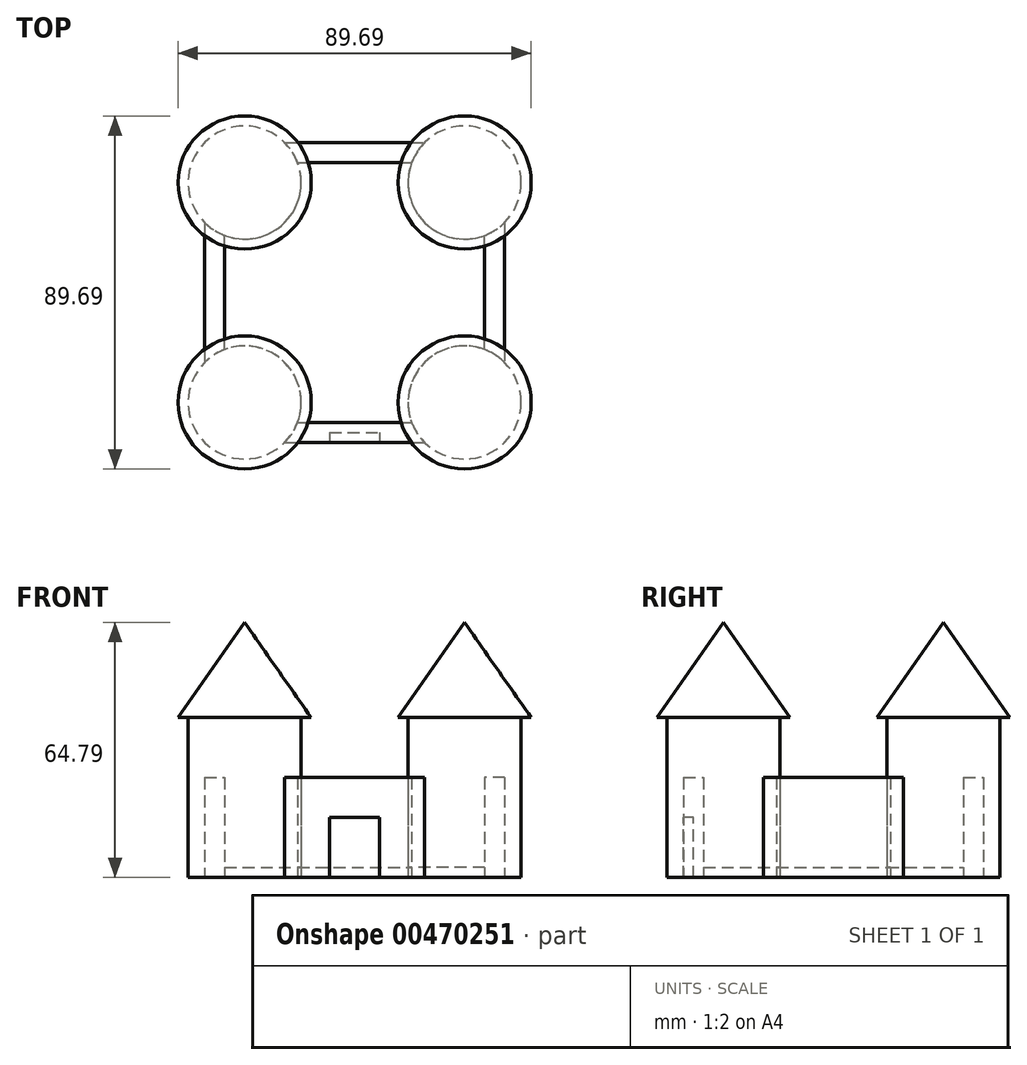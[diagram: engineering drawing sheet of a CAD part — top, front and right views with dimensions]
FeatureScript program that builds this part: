
annotation { "Feature Type Name" : "Feature", "Feature Type Description" : "" }
export const myFeature = defineFeature(function(context is Context, id is Id, definition is map)
    precondition{}
    {
        {
            var Q0;
            Q0=qCreatedBy(makeId("Top.planeOp"),FACE);
            var sketch = newSketch(context, id + "F0", { "sketchPlane" : qUnion([Q0])});
            skLineSegment(sketch, "E0.bottom", {"start": v(-37.26, 36.88) * mm, "end": v(38.94, 36.88) * mm});
            skLineSegment(sketch, "E0.top", {"start": v(-37.26, -39.32) * mm, "end": v(38.94, -39.32) * mm});
            skLineSegment(sketch, "E0.left", {"start": v(-37.26, 36.88) * mm, "end": v(-37.26, -39.32) * mm});
            skLineSegment(sketch, "E0.right", {"start": v(38.94, 36.88) * mm, "end": v(38.94, -39.32) * mm});
            skCircle(sketch, "E1", {"center": v(-27.1, 26.72) * mm, "radius": 14.37 * mm});
            skPoint(sketch, "E1.second.point", {"position": v(-37.26, 16.56) * mm});
            skPoint(sketch, "E1.third.point", {"position": v(-16.94, 36.88) * mm});
            skCircle(sketch, "E2", {"center": v(-27.1, -29.16) * mm, "radius": 14.37 * mm});
            skPoint(sketch, "E2.second.point", {"position": v(-37.26, -19) * mm});
            skPoint(sketch, "E2.third.point", {"position": v(-16.94, -39.32) * mm});
            skCircle(sketch, "E3", {"center": v(28.78, 26.72) * mm, "radius": 14.37 * mm});
            skPoint(sketch, "E3.second.point", {"position": v(18.62, 36.88) * mm});
            skPoint(sketch, "E3.third.point", {"position": v(38.94, 16.56) * mm});
            skCircle(sketch, "E4", {"center": v(28.78, -29.16) * mm, "radius": 14.37 * mm});
            skPoint(sketch, "E4.second.point", {"position": v(38.94, -19) * mm});
            skPoint(sketch, "E4.third.point", {"position": v(18.62, -39.32) * mm});
            skLineSegment(sketch, "E5", {"start": v(-32.18, -15.72) * mm, "end": v(-32.18, 13.28) * mm});
            skLineSegment(sketch, "E6", {"start": v(-13.66, 31.8) * mm, "end": v(15.34, 31.8) * mm});
            skLineSegment(sketch, "E7", {"start": v(-13.66, -34.24) * mm, "end": v(15.34, -34.24) * mm});
            skLineSegment(sketch, "E8", {"start": v(33.86, -15.72) * mm, "end": v(33.86, 13.28) * mm});
            skSolve(sketch);
        }
        {
            var Q0;
            {var subQ5=sQuery(id+"F0.wireOp",EDGE,"E5");Q0=makeQuery(id+"F0.imprint","IMPRINT",FACE,{"disambiguationData":[TD([[makeQuery(id+"F0.imprint","IMPRINT",EDGE,{"derivedFrom":subQ5}),-1.0]])]});}
            extrude(context, id + "F1", {"entities" : qUnion([Q0]), "depth" : 2.54 * mm});
        }
        {
            var Q0;
            {var subQ5=sQuery(id+"F0.wireOp",EDGE,"E8");Q0=makeQuery(id+"F0.imprint","IMPRINT",FACE,{"disambiguationData":[TD([[makeQuery(id+"F0.imprint","IMPRINT",EDGE,{"derivedFrom":subQ5}),-1.0]])]});}
            var Q1;
            {var subQ5=sQuery(id+"F0.wireOp",EDGE,"E7");Q1=makeQuery(id+"F0.imprint","IMPRINT",FACE,{"disambiguationData":[TD([[makeQuery(id+"F0.imprint","IMPRINT",EDGE,{"derivedFrom":subQ5}),-1.0]])]});}
            var Q2;
            {var subQ5=sQuery(id+"F0.wireOp",EDGE,"E5");Q2=makeQuery(id+"F0.imprint","IMPRINT",FACE,{"disambiguationData":[TD([[makeQuery(id+"F0.imprint","IMPRINT",EDGE,{"derivedFrom":subQ5}),1.0]])]});}
            var Q3;
            {var subQ5=sQuery(id+"F0.wireOp",EDGE,"E6");Q3=makeQuery(id+"F0.imprint","IMPRINT",FACE,{"disambiguationData":[TD([[makeQuery(id+"F0.imprint","IMPRINT",EDGE,{"derivedFrom":subQ5}),1.0]])]});}
            extrude(context, id + "F2", {"entities" : qUnion([Q0, Q1, Q2, Q3]), "depth" : 25.4 * mm});
        }
        {
            var Q0;
            {var subQ0=sQuery(id+"F0.wireOp",EDGE,"E3");var subQ1=sQuery(id+"F0.wireOp",EDGE,"E0.right");var subQ3=makeQuery(id+"F0.imprint","INTERSECT",VERTEX,{"derivedFrom":[subQ1,subQ0]});Q0=makeQuery(id+"F0.imprint","IMPRINT",FACE,{"disambiguationData":[TD([[makeQuery(id+"F0.imprint","IMPRINT",EDGE,{"disambiguationData":[TD([[subQ3,1.0]])],"derivedFrom":subQ1}),1.0]])]});}
            var Q1;
            {var subQ0=sQuery(id+"F0.wireOp",EDGE,"E3");var subQ1=makeQuery(id+"F0.imprint","INTERSECT",VERTEX,{"derivedFrom":[subQ0,sQuery(id+"F0.wireOp",EDGE,"E6")]});Q1=makeQuery(id+"F0.imprint","IMPRINT",FACE,{"disambiguationData":[TD([[makeQuery(id+"F0.imprint","IMPRINT",EDGE,{"disambiguationData":[TD([[subQ1,1.0]])],"derivedFrom":subQ0}),1.0]])]});}
            var Q2;
            {var subQ0=sQuery(id+"F0.wireOp",EDGE,"E3");var subQ1=sQuery(id+"F0.wireOp",EDGE,"E0.bottom");var subQ3=makeQuery(id+"F0.imprint","INTERSECT",VERTEX,{"derivedFrom":[subQ1,subQ0]});Q2=makeQuery(id+"F0.imprint","IMPRINT",FACE,{"disambiguationData":[TD([[makeQuery(id+"F0.imprint","IMPRINT",EDGE,{"disambiguationData":[TD([[subQ3,-1.0]])],"derivedFrom":subQ1}),1.0]])]});}
            var Q3;
            {var subQ0=sQuery(id+"F0.wireOp",EDGE,"E4");var subQ1=sQuery(id+"F0.wireOp",EDGE,"E0.right");var subQ3=makeQuery(id+"F0.imprint","INTERSECT",VERTEX,{"derivedFrom":[subQ1,subQ0]});Q3=makeQuery(id+"F0.imprint","IMPRINT",FACE,{"disambiguationData":[TD([[makeQuery(id+"F0.imprint","IMPRINT",EDGE,{"disambiguationData":[TD([[subQ3,-1.0]])],"derivedFrom":subQ1}),1.0]])]});}
            var Q4;
            {var subQ0=sQuery(id+"F0.wireOp",EDGE,"E4");var subQ1=sQuery(id+"F0.wireOp",EDGE,"E0.top");var subQ3=makeQuery(id+"F0.imprint","INTERSECT",VERTEX,{"derivedFrom":[subQ1,subQ0]});Q4=makeQuery(id+"F0.imprint","IMPRINT",FACE,{"disambiguationData":[TD([[makeQuery(id+"F0.imprint","IMPRINT",EDGE,{"disambiguationData":[TD([[subQ3,-1.0]])],"derivedFrom":subQ1}),-1.0]])]});}
            var Q5;
            {var subQ0=sQuery(id+"F0.wireOp",EDGE,"E4");var subQ2=makeQuery(id+"F0.imprint","INTERSECT",VERTEX,{"derivedFrom":[subQ0,sQuery(id+"F0.wireOp",EDGE,"E8")]});Q5=makeQuery(id+"F0.imprint","IMPRINT",FACE,{"disambiguationData":[TD([[makeQuery(id+"F0.imprint","IMPRINT",EDGE,{"disambiguationData":[TD([[subQ2,1.0]])],"derivedFrom":subQ0}),1.0]])]});}
            var Q6;
            {var subQ0=sQuery(id+"F0.wireOp",EDGE,"E2");var subQ1=sQuery(id+"F0.wireOp",EDGE,"E0.top");var subQ3=makeQuery(id+"F0.imprint","INTERSECT",VERTEX,{"derivedFrom":[subQ1,subQ0]});Q6=makeQuery(id+"F0.imprint","IMPRINT",FACE,{"disambiguationData":[TD([[makeQuery(id+"F0.imprint","IMPRINT",EDGE,{"disambiguationData":[TD([[subQ3,1.0]])],"derivedFrom":subQ1}),-1.0]])]});}
            var Q7;
            {var subQ0=sQuery(id+"F0.wireOp",EDGE,"E2");var subQ4=makeQuery(id+"F0.imprint","INTERSECT",VERTEX,{"derivedFrom":[subQ0,sQuery(id+"F0.wireOp",EDGE,"E5")]});Q7=makeQuery(id+"F0.imprint","IMPRINT",FACE,{"disambiguationData":[TD([[makeQuery(id+"F0.imprint","IMPRINT",EDGE,{"disambiguationData":[TD([[subQ4,-1.0]])],"derivedFrom":subQ0}),1.0]])]});}
            var Q8;
            {var subQ0=sQuery(id+"F0.wireOp",EDGE,"E2");var subQ1=sQuery(id+"F0.wireOp",EDGE,"E0.left");var subQ3=makeQuery(id+"F0.imprint","INTERSECT",VERTEX,{"derivedFrom":[subQ1,subQ0]});Q8=makeQuery(id+"F0.imprint","IMPRINT",FACE,{"disambiguationData":[TD([[makeQuery(id+"F0.imprint","IMPRINT",EDGE,{"disambiguationData":[TD([[subQ3,-1.0]])],"derivedFrom":subQ1}),-1.0]])]});}
            var Q9;
            {var subQ0=sQuery(id+"F0.wireOp",EDGE,"E1");var subQ1=sQuery(id+"F0.wireOp",EDGE,"E0.left");var subQ3=makeQuery(id+"F0.imprint","INTERSECT",VERTEX,{"derivedFrom":[subQ1,subQ0]});Q9=makeQuery(id+"F0.imprint","IMPRINT",FACE,{"disambiguationData":[TD([[makeQuery(id+"F0.imprint","IMPRINT",EDGE,{"disambiguationData":[TD([[subQ3,1.0]])],"derivedFrom":subQ1}),-1.0]])]});}
            var Q10;
            {var subQ0=sQuery(id+"F0.wireOp",EDGE,"E1");var subQ1=makeQuery(id+"F0.imprint","INTERSECT",VERTEX,{"derivedFrom":[subQ0,sQuery(id+"F0.wireOp",EDGE,"E6")]});Q10=makeQuery(id+"F0.imprint","IMPRINT",FACE,{"disambiguationData":[TD([[makeQuery(id+"F0.imprint","IMPRINT",EDGE,{"disambiguationData":[TD([[subQ1,-1.0]])],"derivedFrom":subQ0}),1.0]])]});}
            var Q11;
            {var subQ0=sQuery(id+"F0.wireOp",EDGE,"E1");var subQ1=sQuery(id+"F0.wireOp",EDGE,"E0.bottom");var subQ3=makeQuery(id+"F0.imprint","INTERSECT",VERTEX,{"derivedFrom":[subQ1,subQ0]});Q11=makeQuery(id+"F0.imprint","IMPRINT",FACE,{"disambiguationData":[TD([[makeQuery(id+"F0.imprint","IMPRINT",EDGE,{"disambiguationData":[TD([[subQ3,1.0]])],"derivedFrom":subQ1}),1.0]])]});}
            extrude(context, id + "F3", {"entities" : qUnion([Q0, Q1, Q2, Q3, Q4, Q5, Q6, Q7, Q8, Q9, Q10, Q11]), "depth" : 40.64 * mm});
        }
        {
            var Q0;
            Q0=makeQuery(id+"F3.opExtrude","CAP_FACE",FACE,{"disambiguationData":[OSD([sQuery(id+"F0.wireOp",EDGE,"E2")])],"isStart":false});
            var sketch = newSketch(context, id + "F4", { "sketchPlane" : qUnion([Q0])});
            skCircle(sketch, "E9", {"center": v(-27.1, -29.16) * mm, "radius": 16.9 * mm});
            skSolve(sketch);
        }
        {
            var Q0;
            Q0=qSketchRegion(id+"F4",true);
            extrude(context, id + "F5", {"entities" : qUnion([Q0]), "operationType" : NewBodyOperationType.ADD, "depth" : 25.4 * mm, "hasDraft" : true, "draftAngle" : 35 * degree, "draftPullDirection" : true});
        }
        {
            var Q0;
            Q0=makeQuery(id+"F3.opExtrude","CAP_FACE",FACE,{"disambiguationData":[OSD([sQuery(id+"F0.wireOp",EDGE,"E1")])],"isStart":false});
            var sketch = newSketch(context, id + "F6", { "sketchPlane" : qUnion([Q0])});
            skCircle(sketch, "E10", {"center": v(-27.1, 26.72) * mm, "radius": 16.9 * mm});
            skSolve(sketch);
        }
        {
            var Q0;
            Q0=qSketchRegion(id+"F6",true);
            extrude(context, id + "F7", {"entities" : qUnion([Q0]), "operationType" : NewBodyOperationType.ADD, "depth" : 25.4 * mm, "hasDraft" : true, "draftAngle" : 35 * degree, "draftPullDirection" : true});
        }
        {
            var Q0;
            Q0=makeQuery(id+"F3.opExtrude","CAP_FACE",FACE,{"disambiguationData":[OSD([sQuery(id+"F0.wireOp",EDGE,"E3")])],"isStart":false});
            var sketch = newSketch(context, id + "F8", { "sketchPlane" : qUnion([Q0])});
            skCircle(sketch, "E11", {"center": v(28.78, 26.72) * mm, "radius": 16.9 * mm});
            skSolve(sketch);
        }
        {
            var Q0;
            Q0=qSketchRegion(id+"F8",true);
            extrude(context, id + "F9", {"entities" : qUnion([Q0]), "operationType" : NewBodyOperationType.ADD, "depth" : 25.4 * mm, "hasDraft" : true, "draftAngle" : 35 * degree, "draftPullDirection" : true});
        }
        {
            var Q0;
            Q0=makeQuery(id+"F3.opExtrude","CAP_FACE",FACE,{"disambiguationData":[OSD([sQuery(id+"F0.wireOp",EDGE,"E4")])],"isStart":false});
            var sketch = newSketch(context, id + "F10", { "sketchPlane" : qUnion([Q0])});
            skCircle(sketch, "E12", {"center": v(28.78, -29.16) * mm, "radius": 16.9 * mm});
            skSolve(sketch);
        }
        {
            var Q0;
            Q0=qSketchRegion(id+"F10",true);
            extrude(context, id + "F11", {"entities" : qUnion([Q0]), "operationType" : NewBodyOperationType.ADD, "depth" : 25.4 * mm, "hasDraft" : true, "draftAngle" : 35 * degree, "draftPullDirection" : true});
        }
        {
            var Q0;
            Q0=makeQuery(id+"F2.opExtrude","SWEPT_FACE",FACE,{"disambiguationData":[OSD([sQuery(id+"F0.wireOp",EDGE,"E0.top")])]});
            var sketch = newSketch(context, id + "F12", { "sketchPlane" : qUnion([Q0])});
            skLineSegment(sketch, "E13.bottom", {"start": v(-5.51, 0) * mm, "end": v(7.19, 0) * mm});
            skLineSegment(sketch, "E13.top", {"start": v(-5.51, 15.24) * mm, "end": v(7.19, 15.24) * mm});
            skLineSegment(sketch, "E13.left", {"start": v(-5.51, 0) * mm, "end": v(-5.51, 15.24) * mm});
            skLineSegment(sketch, "E13.right", {"start": v(7.19, 0) * mm, "end": v(7.19, 15.24) * mm});
            skSolve(sketch);
        }
        {
            var Q0;
            Q0=makeQuery(id+"F12.imprint","IMPRINT",FACE,{"disambiguationData":[TD([[makeQuery(id+"F12.imprint","IMPRINT",EDGE,{"derivedFrom":sQuery(id+"F12.wireOp",EDGE,"E13.bottom")}),1.0]])]});
            extrude(context, id + "F13", {"entities" : qUnion([Q0]), "operationType" : NewBodyOperationType.REMOVE, "oppositeDirection" : true, "depth" : 2.54 * mm});
        }
    });
